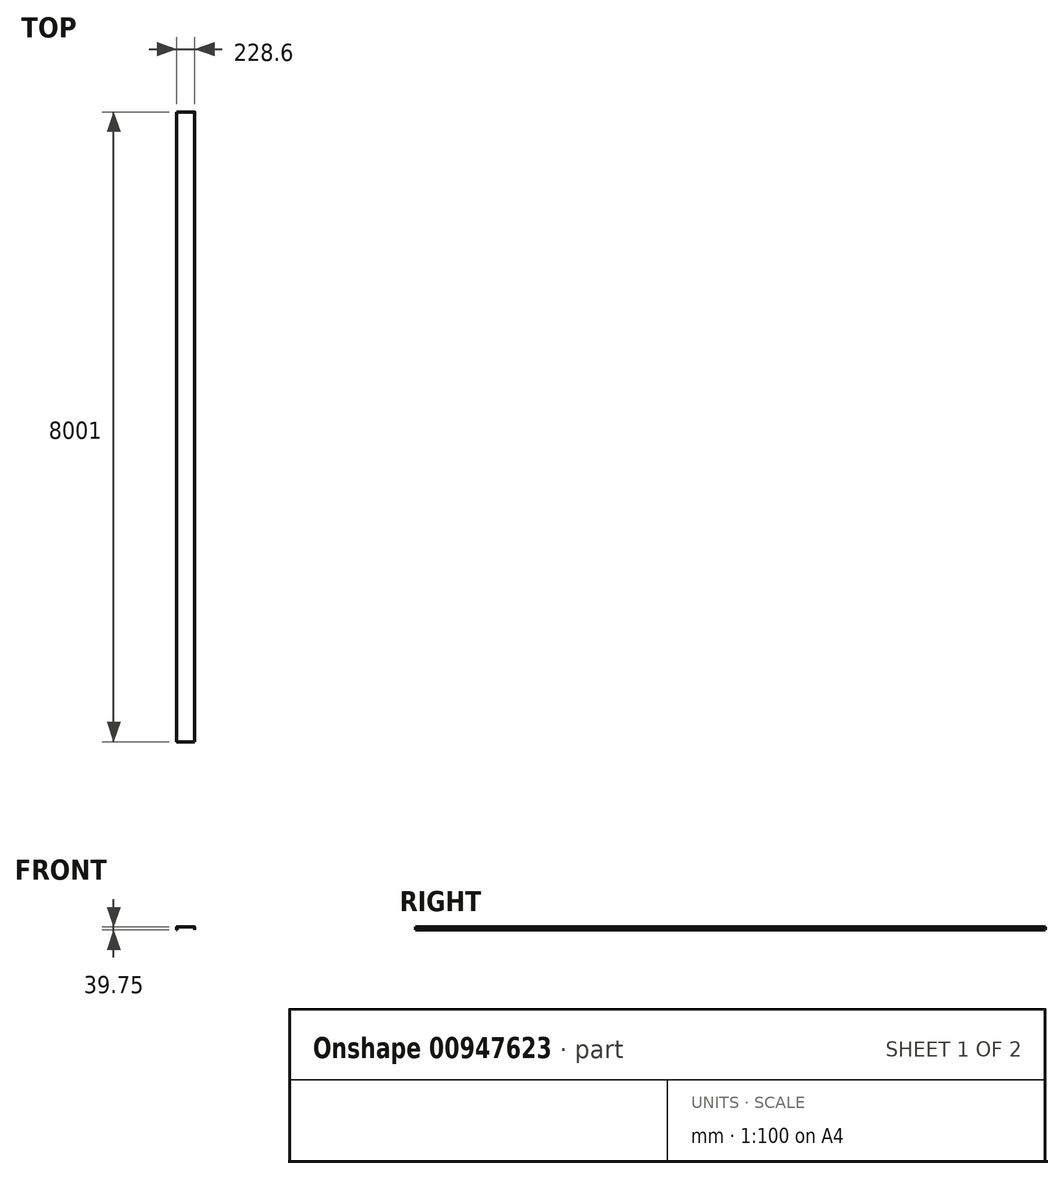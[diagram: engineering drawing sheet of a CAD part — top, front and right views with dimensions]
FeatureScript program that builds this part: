
annotation { "Feature Type Name" : "Feature", "Feature Type Description" : "" }
export const myFeature = defineFeature(function(context is Context, id is Id, definition is map)
    precondition{}
    {
        {
            var Q0;
            Q0=qCreatedBy(makeId("Front.planeOp"),FACE);
            var sketch = newSketch(context, id + "F0", { "sketchPlane" : qUnion([Q0])});
            skLineSegment(sketch, "E0", {"start": v(0, 0) * mm, "end": v(110.5, 0) * mm});
            skLineSegment(sketch, "E1", {"start": v(114.3, -3.81) * mm, "end": v(114.3, -39.75) * mm});
            skLineSegment(sketch, "E2", {"start": v(114.3, -39.75) * mm, "end": v(112.4, -39.75) * mm});
            skLineSegment(sketch, "E3", {"start": v(112.4, -39.75) * mm, "end": v(112.4, -3.8) * mm});
            skLineSegment(sketch, "E4", {"start": v(110.5, -1.9) * mm, "end": v(0, -1.9) * mm});
            skPoint(sketch, "E5.visualSharp", {"position": v(112.4, -1.9) * mm});
            skArc(sketch, "E5.filletArc", {"start": v(112.4, -3.8) * mm, "mid": v(111.84, -2.46) * mm, "end": v(110.5, -1.9) * mm});
            skPoint(sketch, "E6.visualSharp", {"position": v(114.3, 0) * mm});
            skArc(sketch, "E6.filletArc", {"start": v(114.3, -3.8) * mm, "mid": v(113.18, -1.12) * mm, "end": v(110.5, 0) * mm});
            skArc(sketch, "E7.MirrorCS", {"start": v(-112.4, -3.8) * mm, "mid": v(-111.84, -2.46) * mm, "end": v(-110.5, -1.9) * mm});
            skLineSegment(sketch, "E8.MirrorCS", {"start": v(-114.3, -39.75) * mm, "end": v(-112.4, -39.75) * mm});
            skArc(sketch, "E9.MirrorCS", {"start": v(-114.3, -3.8) * mm, "mid": v(-113.18, -1.12) * mm, "end": v(-110.5, 0) * mm});
            skPoint(sketch, "E10.MirrorP", {"position": v(-112.4, -1.9) * mm});
            skLineSegment(sketch, "E11.MirrorCS", {"start": v(0, 0) * mm, "end": v(-110.5, 0) * mm});
            skLineSegment(sketch, "E12.MirrorCS", {"start": v(-110.5, -1.9) * mm, "end": v(0, -1.9) * mm});
            skPoint(sketch, "E13.MirrorP", {"position": v(-114.3, 0) * mm});
            skLineSegment(sketch, "E14.MirrorCS", {"start": v(-114.3, -3.81) * mm, "end": v(-114.3, -39.75) * mm});
            skLineSegment(sketch, "E15.MirrorCS", {"start": v(-112.4, -39.75) * mm, "end": v(-112.4, -3.8) * mm});
            skSolve(sketch);
        }
        {
            var Q0;
            Q0=makeQuery(id+"F0.imprint","IMPRINT",FACE,{"disambiguationData":[TD([[makeQuery(id+"F0.imprint","IMPRINT",EDGE,{"derivedFrom":sQuery(id+"F0.wireOp",EDGE,"E0")}),-1.0]])]});
            extrude(context, id + "F1", {"entities" : qUnion([Q0]), "depth" : 8001 * mm, "offsetDistance" : 25.4 * mm});
        }
    });
